# Revit family: Desk_Screens-Teknion-CQCFD_Routes_Smooth_Felt_Desk_Edge_Screen-R2019
name_source: partatom
category: Furniture
units: mm (PartAtom-declared; Revit-internal decimal feet)

## family parameters
Always vertical = Yes
Cut with Voids When Loaded = No
OmniClass Number = 23.40.20.00
OmniClass Title = General Furniture and Specialties
Room Calculation Point = No
Shared = Yes
Work Plane-Based = No

## types (3) — shared parameters
Assembly Code = E2020200
Manufacturer = Teknion
Manufacturer Fax = 416.661.4586
Part Number = CQCFD
Product Documentation Link = https://assets.teknion.com
Product Line = Routes
Product Page URL = https://www.teknion.com
Series = Routes
Sustainability Data = https://www.teknion.com
URL = www.teknion.com
Unit Weight URL = http://www.teknion.com
Warranty = http://www.teknion.com

## per-type parameters (varying)
| type | Datum Height | Description | Model | Modesty Base Height |
| 47" Datum Height, Slim Modesty Height | 47 " | Smooth Felt Desk End Screen, 47" Datum Height, Slim Modesty Height (24") | CQCFD47L__ | 24 " |
| 42" Datum Height, Slim Modesty Height | 42 " | Smooth Felt Desk End Screen, 42" Datum Height, Slim Modesty Height (24") | CQCFD42L__ | 24 " |
| 42" Datum Height, Semi Modesty Height | 42 " | Smooth Felt Desk End Screen, 42" Datum Height, Semi Modesty Height (19") | CQCFD42T__ | 19 " |

## geometry (parser evidence)
native form markers: Sweep x6
no freeform markers — native parametric forms only
